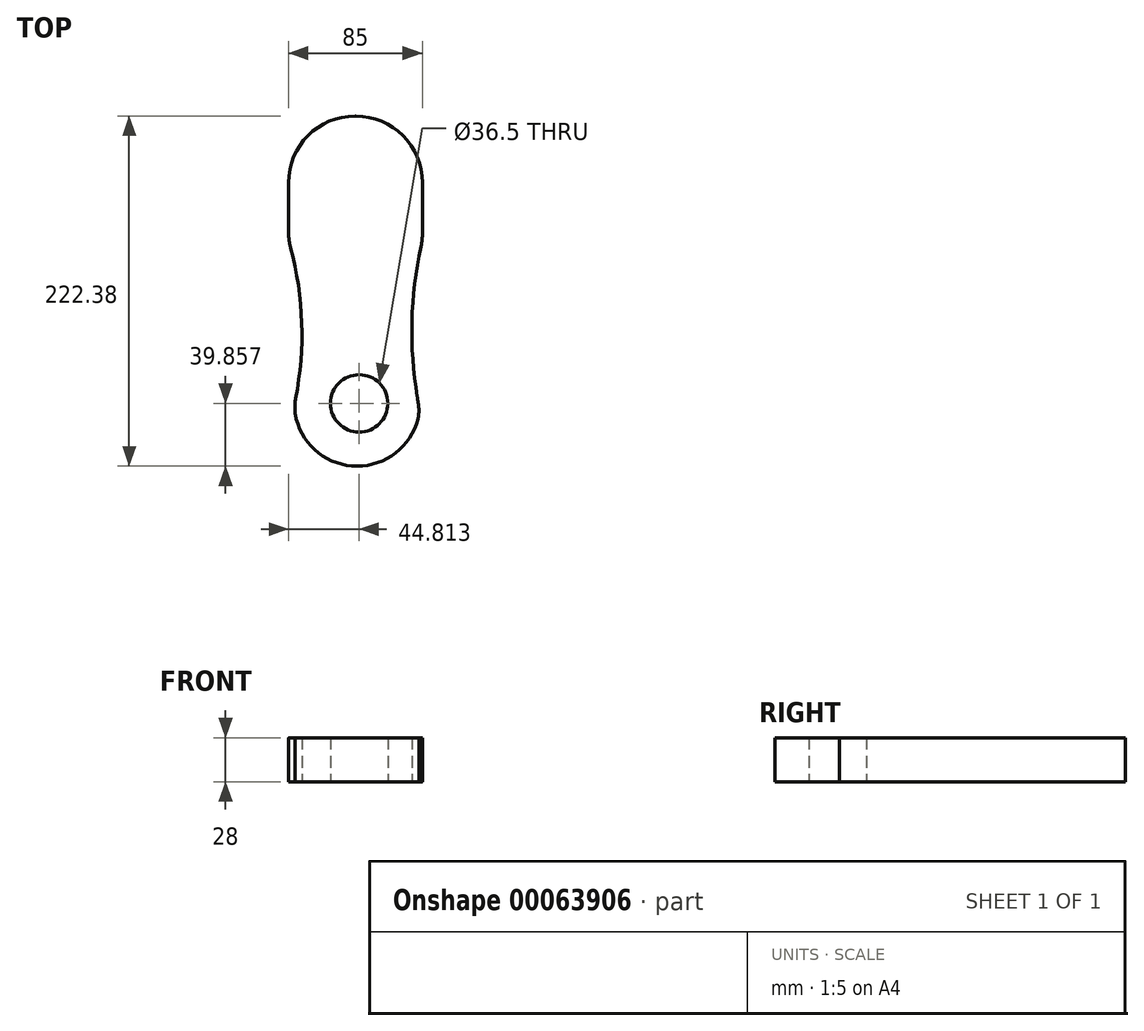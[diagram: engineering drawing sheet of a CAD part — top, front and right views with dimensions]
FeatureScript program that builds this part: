
annotation { "Feature Type Name" : "Feature", "Feature Type Description" : "" }
export const myFeature = defineFeature(function(context is Context, id is Id, definition is map)
    precondition{}
    {
        {
            var Q0;
            Q0=qCreatedBy(makeId("Top.planeOp"),FACE);
            var sketch = newSketch(context, id + "F0", { "sketchPlane" : qUnion([Q0])});
            skLineSegment(sketch, "E0", {"start": v(23.15, 114.06) * mm, "end": v(23.55, 114.06) * mm});
            skPoint(sketch, "E1", {"position": v(42.26, -21.75) * mm});
            skPoint(sketch, "E2", {"position": v(49.28, 44.2) * mm});
            skPoint(sketch, "E3", {"position": v(65.85, 114.06) * mm});
            skPoint(sketch, "E4", {"position": v(28.88, 11.34) * mm});
            skPoint(sketch, "E5", {"position": v(-28.99, -21.75) * mm});
            skPoint(sketch, "E6", {"position": v(-8.42, 11.34) * mm});
            skPoint(sketch, "E7", {"position": v(-28.92, 44.2) * mm});
            skPoint(sketch, "E8", {"position": v(-19.15, 114.06) * mm});
            skArc(sketch, "E9.filletArc", {"start": v(34.48, -104.74) * mm, "mid": v(34.61, -103.95) * mm, "end": v(34.72, -103.15) * mm});
            skArc(sketch, "E10.filletArc", {"start": v(45.94, -118.14) * mm, "mid": v(46.05, -116.93) * mm, "end": v(46.08, -115.72) * mm});
            skArc(sketch, "E11.filletArc", {"start": v(46.04, -106.23) * mm, "mid": v(46.07, -105.54) * mm, "end": v(46.08, -104.86) * mm});
            skArc(sketch, "E12", {"start": v(-14.62, -65.2) * mm, "mid": v(-10.8, -17.27) * mm, "end": v(-17.8, 30.3) * mm});
            skLineSegment(sketch, "E13", {"start": v(-19.15, 71.76) * mm, "end": v(-19.15, 40.56) * mm});
            skLineSegment(sketch, "E14", {"start": v(65.85, 71.76) * mm, "end": v(65.85, 39.6) * mm});
            skArc(sketch, "E15", {"start": v(64.93, 31.06) * mm, "mid": v(59.22, -16.45) * mm, "end": v(62.6, -64.18) * mm});
            skArc(sketch, "E16.filletArc", {"start": v(23.15, 114.06) * mm, "mid": v(-6.76, 101.67) * mm, "end": v(-19.15, 71.76) * mm});
            skArc(sketch, "E17.filletArc", {"start": v(65.85, 71.76) * mm, "mid": v(53.46, 101.67) * mm, "end": v(23.55, 114.06) * mm});
            skPoint(sketch, "E18.visualSharp", {"position": v(-19.15, 35.11) * mm});
            skArc(sketch, "E18.filletArc", {"start": v(-19.15, 40.56) * mm, "mid": v(-18.81, 35.39) * mm, "end": v(-17.8, 30.3) * mm});
            skPoint(sketch, "E19.visualSharp", {"position": v(65.85, 35.11) * mm});
            skArc(sketch, "E19.filletArc", {"start": v(64.93, 31.06) * mm, "mid": v(65.62, 35.3) * mm, "end": v(65.85, 39.6) * mm});
            skPoint(sketch, "E20.visualSharp", {"position": v(-17.38, -77.46) * mm});
            skArc(sketch, "E21.filletArc", {"start": v(-14.62, -65.2) * mm, "mid": v(-15.16, -71.8) * mm, "end": v(-14.25, -78.34) * mm});
            skArc(sketch, "E22.filletArc", {"start": v(62.98, -67.6) * mm, "mid": v(62.85, -65.88) * mm, "end": v(62.6, -64.18) * mm});
            skArc(sketch, "E23", {"start": v(62.98, -78.34) * mm, "mid": v(63.64, -72.97) * mm, "end": v(62.98, -67.6) * mm});
            skArc(sketch, "E24", {"start": v(-14.25, -78.34) * mm, "mid": v(24.37, -108.32) * mm, "end": v(62.98, -78.34) * mm});
            skCircle(sketch, "E25", {"center": v(25.66, -68.46) * mm, "radius": 18.25 * mm});
            skPoint(sketch, "E26", {"position": v(-8.88, 30.3) * mm});
            skPoint(sketch, "E27", {"position": v(-8.42, -65.2) * mm});
            skPoint(sketch, "E28", {"position": v(56.31, -69.14) * mm});
            skPoint(sketch, "E29", {"position": v(24.56, -42.48) * mm});
            skPoint(sketch, "E30", {"position": v(26.08, -108.28) * mm});
            skPoint(sketch, "E31", {"position": v(25.66, -60.62) * mm});
            skPoint(sketch, "E32", {"position": v(7.58, -70.95) * mm});
            skPoint(sketch, "E33", {"position": v(43.88, -67.35) * mm});
            skSolve(sketch);
        }
        {
            var Q0;
            {var subQ2=sQuery(id+"F0.wireOp",EDGE,"D9fyI4fW-Rz2T-4jqM-XK19-fTbyvRjLKxcn");Q0=makeQuery(id+"F0.imprint","IMPRINT",FACE,{"disambiguationData":[TD([[makeQuery(id+"F0.imprint","IMPRINT",EDGE,{"derivedFrom":subQ2}),-1.0]])]});}
            var Q1;
            {var subQ0=sQuery(id+"F0.wireOp",EDGE,"E0");Q1=makeQuery(id+"F0.imprint","IMPRINT",FACE,{"disambiguationData":[TD([[makeQuery(id+"F0.imprint","IMPRINT",EDGE,{"derivedFrom":subQ0}),-1.0]])]});}
            extrude(context, id + "F1", {"entities" : qUnion([Q0, Q1]), "depth" : 28 * mm});
        }
    });
